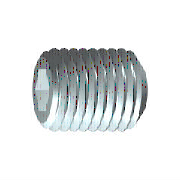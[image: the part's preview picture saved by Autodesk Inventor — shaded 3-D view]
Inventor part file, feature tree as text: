
AUTODESK INVENTOR PART (.ipt)
format: ipt  version: 2017.3 (Build 213256000, 256)  size: 163,840 bytes
history: native  units: mm (DEFAULTED — no unit token found)
features: sketch x2, extrude x1, other x1, plane x1
ambient origin geometry x8: Origin, YZ Plane, XZ Plane, XY Plane, X Axis, Y Axis, Z Axis, Center Point
bodies: Solid1 (feature_tree), Body (feature_tree)
feature tree (5):
  extrude  "Slot"  TaperAngle=60.0deg  [1 undecoded]
  other  "Work Axis1"
  plane  "Work Plane1"
  sketch  "Sketch1"  dims[d0=1.8mm d1=60.0deg]
  sketch  "Sketch2"  dims[d2=4.0mm d3=2.309401mm d6=90.0deg d4=0.0mm d5=4.0mm d7=0.429415mm d8=45.0deg d21=10.0mm d9=0.0mm d11=4.0mm d12=0.0mm d13=0.429415mm d14=45.0deg d15=0.0mm d29=0.429415mm d30=0.429415mm d31=0.0mm]
note: 1 required parameter value undecoded (feature->parameter linkage not recoverable at this tier; creation-order binding heuristic only, values carry confidence <= 0.55)
